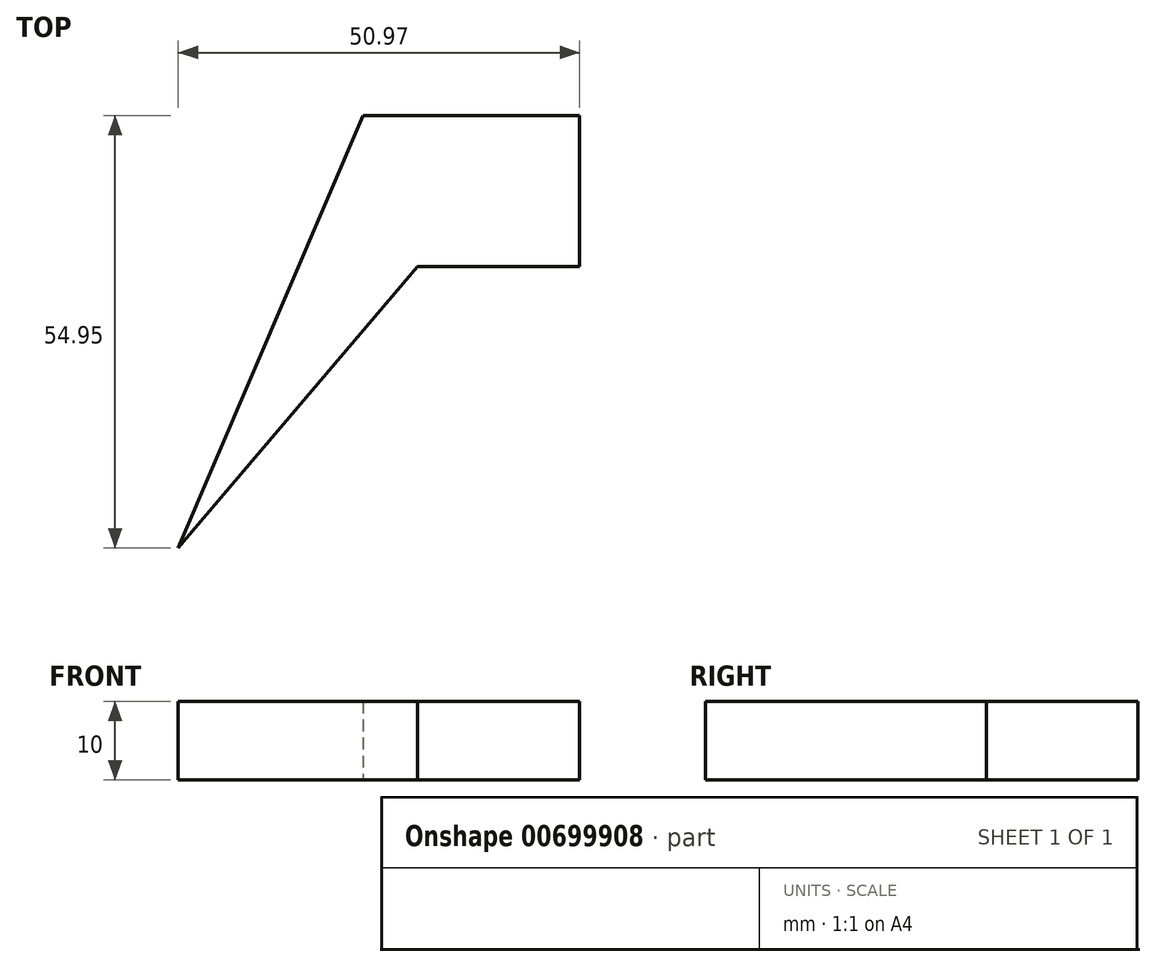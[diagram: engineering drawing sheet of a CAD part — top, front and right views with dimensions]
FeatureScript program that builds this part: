
annotation { "Feature Type Name" : "Feature", "Feature Type Description" : "" }
export const myFeature = defineFeature(function(context is Context, id is Id, definition is map)
    precondition{}
    {
        {
            var Q0;
            Q0=qCreatedBy(makeId("Top.planeOp"),FACE);
            var sketch = newSketch(context, id + "F0", { "sketchPlane" : qUnion([Q0])});
            skLineSegment(sketch, "E0.bottom", {"start": v(-30.37, 30.68) * mm, "end": v(32.2, 30.68) * mm});
            skLineSegment(sketch, "E0.top", {"start": v(-30.37, -24.27) * mm, "end": v(32.2, -24.27) * mm});
            skLineSegment(sketch, "E0.left", {"start": v(-30.37, 30.68) * mm, "end": v(-30.37, -24.27) * mm});
            skLineSegment(sketch, "E0.right", {"start": v(32.2, 30.68) * mm, "end": v(32.2, -24.27) * mm});
            skLineSegment(sketch, "E1", {"start": v(32.2, 11.45) * mm, "end": v(0, 11.45) * mm});
            skLineSegment(sketch, "E2", {"start": v(0, 11.45) * mm, "end": v(-30.37, -24.27) * mm});
            skLineSegment(sketch, "E3", {"start": v(-6.87, 30.68) * mm, "end": v(-30.37, -24.27) * mm});
            skLineSegment(sketch, "E4", {"start": v(20.6, 11.45) * mm, "end": v(20.6, 30.68) * mm});
            skSolve(sketch);
        }
        {
            var Q0;
            {var subQ1=sQuery(id+"F0.wireOp",EDGE,"E2");Q0=makeQuery(id+"F0.imprint","IMPRINT",FACE,{"disambiguationData":[TD([[makeQuery(id+"F0.imprint","IMPRINT",EDGE,{"derivedFrom":subQ1}),-1.0]])]});}
            extrude(context, id + "F1", {"entities" : qUnion([Q0]), "depth" : 10 * mm, "offsetDistance" : 25 * mm});
        }
    });
